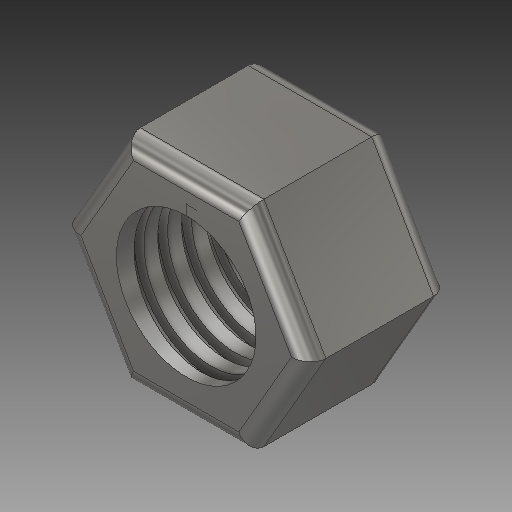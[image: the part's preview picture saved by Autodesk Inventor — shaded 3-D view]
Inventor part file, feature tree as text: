
AUTODESK INVENTOR PART (.ipt)
format: ipt  version: 2019 (Build 230136000, 136)  size: 365,056 bytes
history: native  units: mm
features: sketch x3, extrude x2, fillet x1, helix x1
ambient origin geometry x8: Origin, YZ Plane, XZ Plane, XY Plane, X Axis, Y Axis, Z Axis, Center Point
bodies: Solid1 (feature_tree)
feature tree (7):
  extrude  "Extrusion1"  Depth=5.369358mm
  extrude  "Extrusion2"  Depth=7.0mm
  fillet  "Fillet1"  Radius=7.0mm
  helix  "Coil1"  [1 undecoded]
  sketch  "Sketch1"  dims[d0=12.4mm d1=5.369358mm]
  sketch  "Sketch2"  dims[d2=7.0mm d3=0.0mm d4=7.0mm d5=7.0mm d6=0.0mm d7=0.8mm]
  sketch  "Sketch3"  dims[d8=0.5mm d9=0.5mm d10=10.0mm d11=7.0mm d12=58.9mm d13=0.0mm d14=90.0deg d15=90.0deg d16=0.0mm d17=0.0mm]
note: 1 required parameter value undecoded (feature->parameter linkage not recoverable at this tier; creation-order binding heuristic only, values carry confidence <= 0.55)
